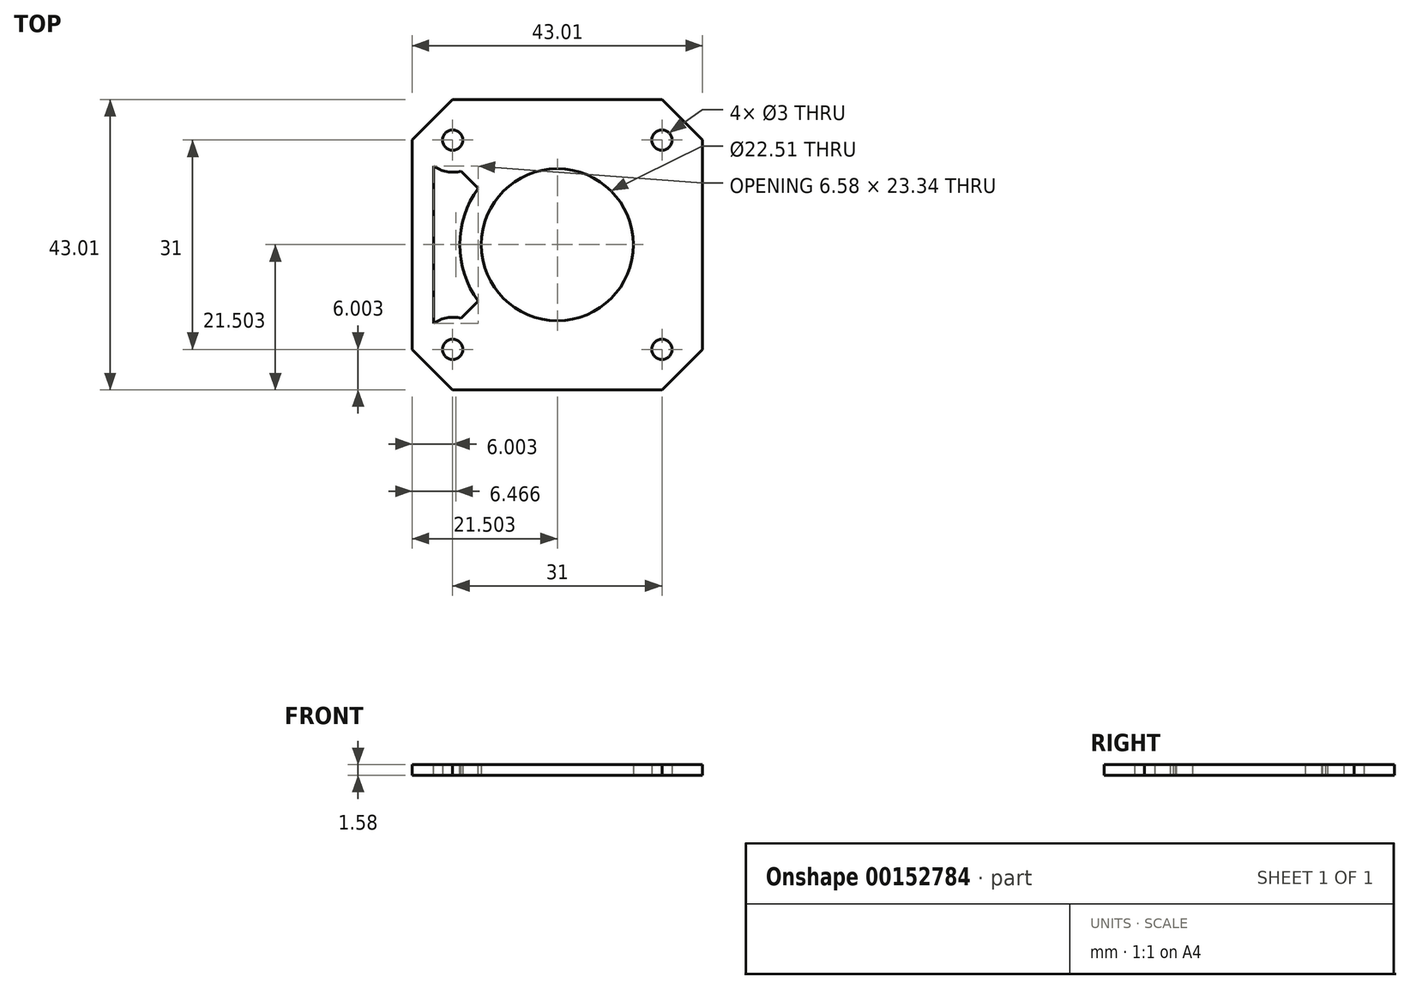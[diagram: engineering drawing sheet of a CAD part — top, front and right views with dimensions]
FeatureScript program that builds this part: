
annotation { "Feature Type Name" : "Feature", "Feature Type Description" : "" }
export const myFeature = defineFeature(function(context is Context, id is Id, definition is map)
    precondition{}
    {
        {
            var Q0;
            Q0=qCreatedBy(makeId("Top.planeOp"),FACE);
            var sketch = newSketch(context, id + "F0", { "sketchPlane" : qUnion([Q0])});
            skLineSegment(sketch, "E0.bottom", {"start": v(0, 0) * mm, "end": v(43, 0) * mm});
            skLineSegment(sketch, "E0.top", {"start": v(0, 43) * mm, "end": v(43, 43) * mm});
            skLineSegment(sketch, "E0.left", {"start": v(0, 0) * mm, "end": v(0, 43) * mm});
            skLineSegment(sketch, "E0.right", {"start": v(43, 0) * mm, "end": v(43, 43) * mm});
            skLineSegment(sketch, "E1", {"start": v(21.5, 43) * mm, "end": v(21.5, 0) * mm, "construction": true});
            skLineSegment(sketch, "E2.bottom", {"start": v(37, 37) * mm, "end": v(6, 37) * mm, "construction": true});
            skLineSegment(sketch, "E2.top", {"start": v(37, 6) * mm, "end": v(6, 6) * mm, "construction": true});
            skLineSegment(sketch, "E2.left", {"start": v(37, 37) * mm, "end": v(37, 6) * mm, "construction": true});
            skLineSegment(sketch, "E2.right", {"start": v(6, 37) * mm, "end": v(6, 6) * mm, "construction": true});
            skPoint(sketch, "E2.middle", {"position": v(21.5, 21.5) * mm});
            skCircle(sketch, "E3", {"center": v(6, 37) * mm, "radius": 1.5 * mm});
            skCircle(sketch, "E4", {"center": v(37, 37) * mm, "radius": 1.5 * mm});
            skCircle(sketch, "E5", {"center": v(21.5, 21.5) * mm, "radius": 11.25 * mm});
            skCircle(sketch, "E6", {"center": v(37, 6) * mm, "radius": 1.5 * mm});
            skCircle(sketch, "E7", {"center": v(6, 6) * mm, "radius": 1.5 * mm});
            skSolve(sketch);
        }
        {
            var Q0;
            Q0=makeQuery(id+"F0.imprint","IMPRINT",FACE,{"disambiguationData":[TD([[makeQuery(id+"F0.imprint","IMPRINT",EDGE,{"derivedFrom":sQuery(id+"F0.wireOp",EDGE,"E0.bottom")}),1.0]])]});
            extrude(context, id + "F1", {"entities" : qUnion([Q0]), "depth" : 1.58 * mm});
        }
        {
            var Q0;
            Q0=makeQuery(id+"F1.opExtrude","SWEPT_EDGE",EDGE,{"disambiguationData":[OSD([sQuery(id+"F0.wireOp",EDGE,"E0.bottom"),sQuery(id+"F0.wireOp",EDGE,"E0.left")])]});
            var Q1;
            Q1=makeQuery(id+"F1.opExtrude","SWEPT_EDGE",EDGE,{"disambiguationData":[OSD([sQuery(id+"F0.wireOp",EDGE,"E0.top"),sQuery(id+"F0.wireOp",EDGE,"E0.left")])]});
            var Q2;
            Q2=makeQuery(id+"F1.opExtrude","SWEPT_EDGE",EDGE,{"disambiguationData":[OSD([sQuery(id+"F0.wireOp",EDGE,"E0.bottom"),sQuery(id+"F0.wireOp",EDGE,"E0.right")])]});
            var Q3;
            Q3=makeQuery(id+"F1.opExtrude","SWEPT_EDGE",EDGE,{"disambiguationData":[OSD([sQuery(id+"F0.wireOp",EDGE,"E0.top"),sQuery(id+"F0.wireOp",EDGE,"E0.right")])]});
            chamfer(context, id + "F2", {"entities" : qUnion([Q0, Q1, Q2, Q3]), "width" : 6 * mm, "tangentPropagation" : true});
        }
        {
            var Q0;
            Q0=makeQuery(id+"F1.opExtrude","CAP_FACE",FACE,{"disambiguationData":[OSD([sQuery(id+"F0.wireOp",EDGE,"E0.bottom"),sQuery(id+"F0.wireOp",EDGE,"E0.top"),sQuery(id+"F0.wireOp",EDGE,"E0.left"),sQuery(id+"F0.wireOp",EDGE,"E0.right"),sQuery(id+"F0.wireOp",EDGE,"E3"),sQuery(id+"F0.wireOp",EDGE,"E4"),sQuery(id+"F0.wireOp",EDGE,"E5"),sQuery(id+"F0.wireOp",EDGE,"E6"),sQuery(id+"F0.wireOp",EDGE,"E7")])],"isStart":false});
            var sketch = newSketch(context, id + "F3", { "sketchPlane" : qUnion([Q0])});
            skLineSegment(sketch, "E8", {"start": v(6, 37) * mm, "end": v(8.92, 34.09) * mm, "construction": true});
            skLineSegment(sketch, "E9", {"start": v(8.92, 34.09) * mm, "end": v(21.5, 21.5) * mm, "construction": true});
            skLineSegment(sketch, "E10", {"start": v(21.5, 21.5) * mm, "end": v(8.92, 8.92) * mm, "construction": true});
            skLineSegment(sketch, "E11", {"start": v(8.92, 8.92) * mm, "end": v(6, 6) * mm, "construction": true});
            skLineSegment(sketch, "E12", {"start": v(0, 21.5) * mm, "end": v(3.18, 21.5) * mm, "construction": true});
            skLineSegment(sketch, "E13", {"start": v(3.17, 33.17) * mm, "end": v(3.18, 9.83) * mm});
            skLineSegment(sketch, "E14", {"start": v(8.92, 34.09) * mm, "end": v(7.24, 32.4) * mm, "construction": true});
            skLineSegment(sketch, "E15", {"start": v(8.92, 8.92) * mm, "end": v(7.24, 10.6) * mm, "construction": true});
            skLineSegment(sketch, "E16", {"start": v(7.24, 32.4) * mm, "end": v(9.76, 29.88) * mm});
            skLineSegment(sketch, "E17", {"start": v(7.24, 10.6) * mm, "end": v(9.76, 13.12) * mm});
            skArc(sketch, "E18", {"start": v(3.17, 33.17) * mm, "mid": v(5.12, 32.32) * mm, "end": v(7.24, 32.4) * mm});
            skArc(sketch, "E19", {"start": v(9.76, 29.88) * mm, "mid": v(7.07, 21.5) * mm, "end": v(9.76, 13.12) * mm});
            skArc(sketch, "E20", {"start": v(7.24, 10.6) * mm, "mid": v(5.12, 10.68) * mm, "end": v(3.17, 9.83) * mm});
            skSolve(sketch);
        }
        {
            var Q0;
            Q0=qSketchRegion(id+"F3",true);
            var Q1;
            Q1=makeQuery(id+"F1.opExtrude","CAP_FACE",FACE,{"disambiguationData":[OSD([sQuery(id+"F0.wireOp",EDGE,"E0.bottom"),sQuery(id+"F0.wireOp",EDGE,"E0.top"),sQuery(id+"F0.wireOp",EDGE,"E0.left"),sQuery(id+"F0.wireOp",EDGE,"E0.right"),sQuery(id+"F0.wireOp",EDGE,"E3"),sQuery(id+"F0.wireOp",EDGE,"E4"),sQuery(id+"F0.wireOp",EDGE,"E5"),sQuery(id+"F0.wireOp",EDGE,"E6"),sQuery(id+"F0.wireOp",EDGE,"E7")])],"isStart":true});
            extrude(context, id + "F4", {"entities" : qUnion([Q0]), "operationType" : NewBodyOperationType.REMOVE, "endBound" : BoundingType.UP_TO_SURFACE, "oppositeDirection" : true, "endBoundEntityFace" : qUnion([Q1]), "depth" : 25.4 * mm});
        }
    });
